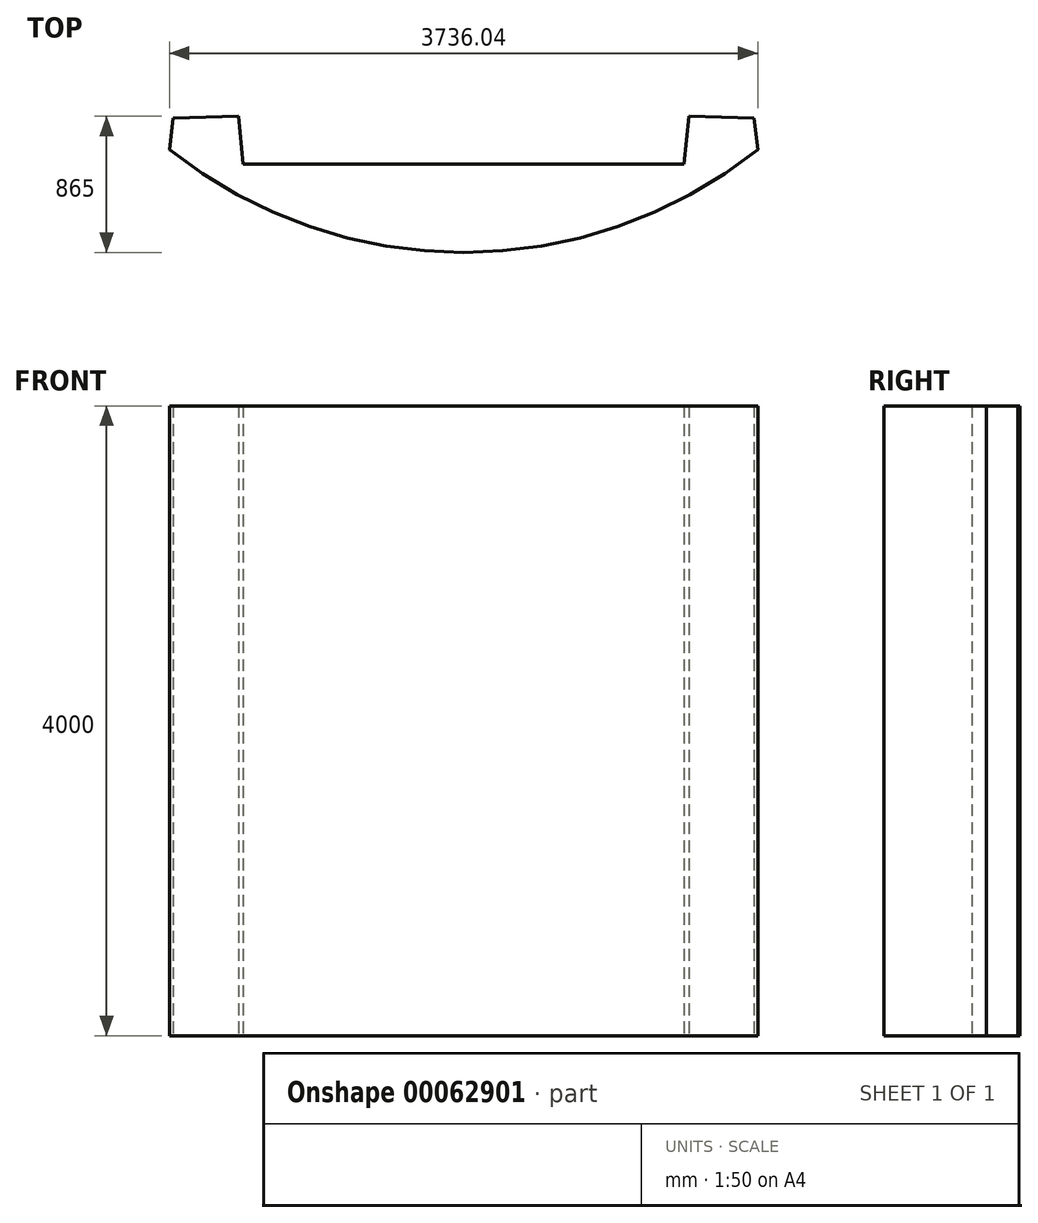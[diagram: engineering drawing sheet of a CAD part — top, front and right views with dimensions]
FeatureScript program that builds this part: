
annotation { "Feature Type Name" : "Feature", "Feature Type Description" : "" }
export const myFeature = defineFeature(function(context is Context, id is Id, definition is map)
    precondition{}
    {
        {
            var Q0;
            Q0=qCreatedBy(makeId("Top.planeOp"),FACE);
            var sketch = newSketch(context, id + "F0", { "sketchPlane" : qUnion([Q0])});
            skCircle(sketch, "E0", {"center": v(0, 0) * mm, "radius": 3000 * mm});
            skLineSegment(sketch, "E1", {"start": v(0, -2440) * mm, "end": v(-1400, -2440) * mm});
            skLineSegment(sketch, "E2", {"start": v(-1430, -2135) * mm, "end": v(-1400, -2440) * mm});
            skLineSegment(sketch, "E3", {"start": v(-1844.87, -2147.45) * mm, "end": v(-1430, -2135) * mm});
            skLineSegment(sketch, "E4", {"start": v(-1868.02, -2347.45) * mm, "end": v(-1844.87, -2147.45) * mm});
            skLineSegment(sketch, "E5.MirrorCS", {"start": v(1868.02, -2347.45) * mm, "end": v(1844.87, -2147.45) * mm});
            skLineSegment(sketch, "E6.MirrorCS", {"start": v(1844.87, -2147.45) * mm, "end": v(1430, -2135) * mm});
            skLineSegment(sketch, "E7.MirrorCS", {"start": v(1430, -2135) * mm, "end": v(1400, -2440) * mm});
            skLineSegment(sketch, "E8.MirrorCS", {"start": v(0, -2440) * mm, "end": v(1400, -2440) * mm});
            skSolve(sketch);
        }
        {
            var Q0;
            Q0=makeQuery(id+"F0.imprint","IMPRINT",FACE,{"disambiguationData":[TD([[makeQuery(id+"F0.imprint","IMPRINT",EDGE,{"derivedFrom":sQuery(id+"F0.wireOp",EDGE,"E1")}),1.0]])]});
            extrude(context, id + "F1", {"entities" : qUnion([Q0]), "depth" : 4000 * mm});
        }
    });
